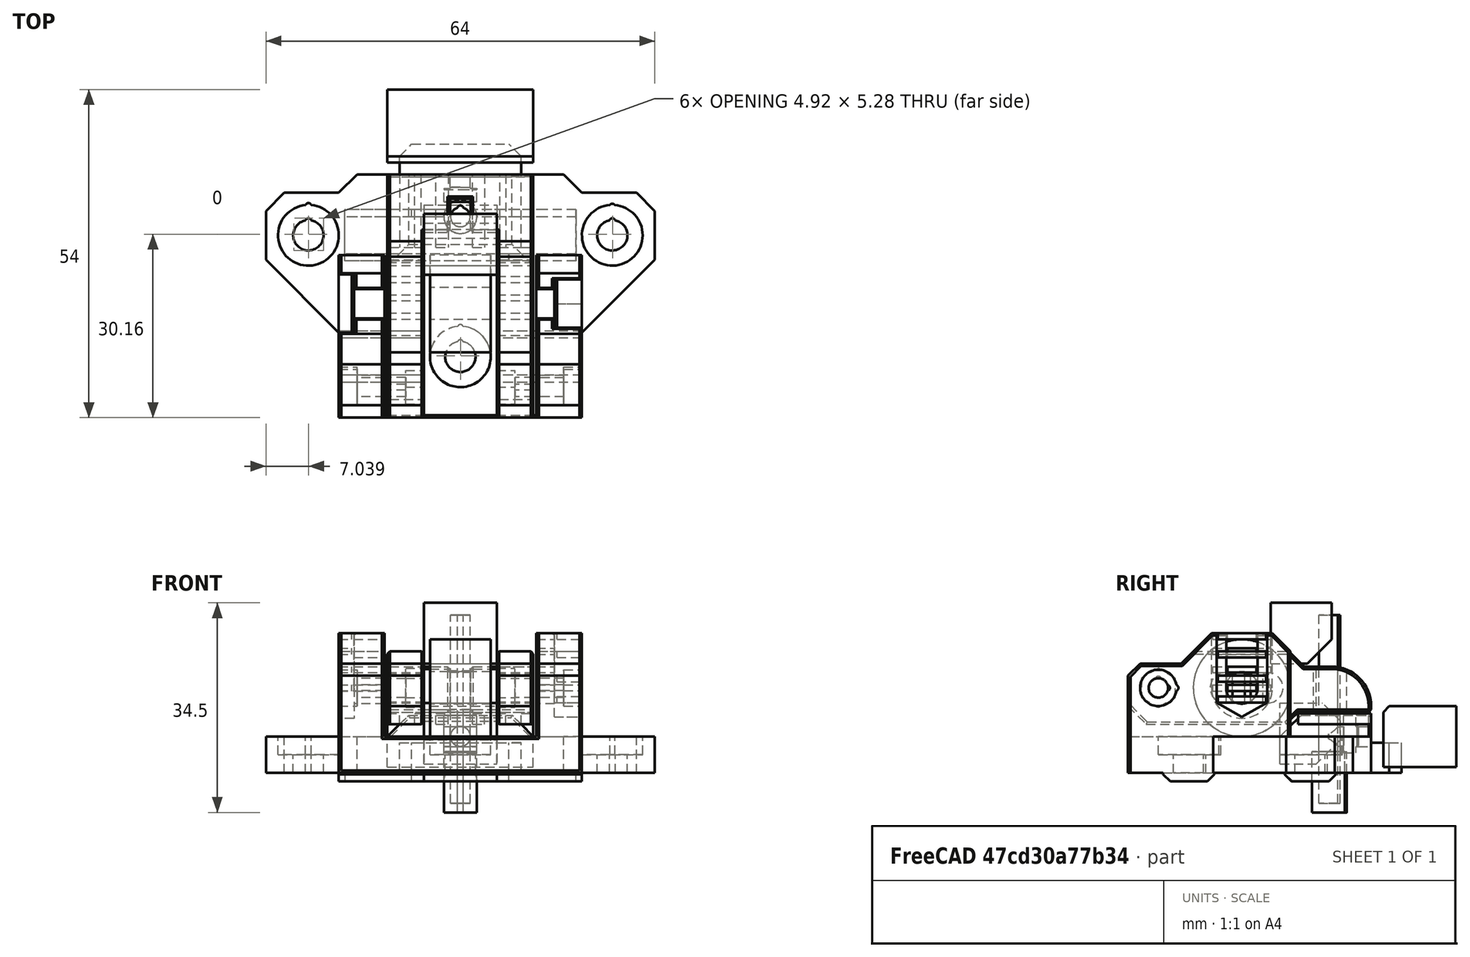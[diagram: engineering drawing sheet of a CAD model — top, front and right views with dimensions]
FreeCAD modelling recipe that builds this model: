
FCSTD DOCUMENT  (FreeCAD 0.18R14555 (Git shallow))
Label: y-idler-10mm-lower-rev
License: All rights reserved
LicenseURL: http://en.wikipedia.org/wiki/All_rights_reserved
objects: Part::Box×69, Part::Cylinder×39, Part::MultiFuse×35, Part::Cut×34, Part::Chamfer×25, Part::Feature×14, Part::Fillet×1
note: 217 computed .brp shape members not serialized (recipe doc carries the construction recipe); baked Part::Feature solids carry a one-line shape summary decoded from their .brp

FEATURE [Part::Box] Box  label="Cube"
  AttacherType = Attacher::AttachEngine3D
  Height = 10
  Length = 40
  Placement = pos=(-20,-20,-10) rot=(0,0,1;0rad)
  Width = 40
FEATURE [Part::Box] Box001  label="Cube001"
  AttacherType = Attacher::AttachEngine3D
  Height = 12
  Length = 6
  Placement = pos=(6,-20,4) rot=(0,0,1;0rad)
  Width = 43
FEATURE [Part::Box] Box002  label="Cube002"
  AttacherType = Attacher::AttachEngine3D
  Height = 12
  Length = 6
  Placement = pos=(-12,-20,4) rot=(0,0,1;0rad)
  Width = 43
FEATURE [Part::Box] Box003  label="Cube003"
  AttacherType = Attacher::AttachEngine3D
  Height = 12
  Length = 12
  Placement = pos=(-6,10.5,3) rot=(0,0,1;0rad)
  Width = 12.5
FEATURE [Part::Cylinder] Cylinder  label="idler"
  Angle = 360
  AttacherType = Attacher::AttachEngine3D
  Height = 10
  Placement = pos=(5,-1.25,10) rot=(0,-1,0;1.5708rad)
  Radius = 8
FEATURE [Part::Cylinder] Cylinder001
  Angle = 360
  AttacherType = Attacher::AttachEngine3D
  Height = 6
  Placement = pos=(6,-2,15) rot=(0,1,0;1.5708rad)
  Radius = 2.5
FEATURE [Part::Cylinder] Cylinder002
  Angle = 360
  AttacherType = Attacher::AttachEngine3D
  Height = 6
  Placement = pos=(-12,5,15) rot=(0,1,0;1.5708rad)
  Radius = 2.5
FEATURE [Part::Cylinder] Cylinder003
  Angle = 360
  AttacherType = Attacher::AttachEngine3D
  Height = 6
  Placement = pos=(-12,-2,15) rot=(0,1,0;1.5708rad)
  Radius = 2.5
FEATURE [Part::Cylinder] Cylinder004
  Angle = 360
  AttacherType = Attacher::AttachEngine3D
  Height = 6
  Placement = pos=(6,5,15) rot=(0,1,0;1.5708rad)
  Radius = 2.5
FEATURE [Part::Box] Box005  label="Cube005"
  AttacherType = Attacher::AttachEngine3D
  Height = 5
  Length = 6
  Placement = pos=(6,-2,12.5) rot=(0,0,1;0rad)
  Width = 7
FEATURE [Part::Box] Box006  label="Cube006"
  AttacherType = Attacher::AttachEngine3D
  Height = 5
  Length = 6
  Placement = pos=(-12,-2,12.5) rot=(0,0,1;0rad)
  Width = 7
FEATURE [Part::MultiFuse] Fusion
  Placement = pos=(0,-2,-5) rot=(0,0,1;0rad)
  Shapes = -> [Box005,Cylinder001,Cylinder004]
FEATURE [Part::MultiFuse] Fusion001
  Placement = pos=(0,-2,-5) rot=(0,0,1;0rad)
  Shapes = -> [Box006,Cylinder003,Cylinder002]
FEATURE [Part::Box] Box007  label="Cube007"
  AttacherType = Attacher::AttachEngine3D
  Height = 12
  Length = 7.5
  Placement = pos=(-20,-20,0) rot=(0,0,1;0rad)
  Width = 11
FEATURE [Part::Box] Box008  label="Cube008"
  AttacherType = Attacher::AttachEngine3D
  Height = 12
  Length = 7.5
  Placement = pos=(12.5,-20,0) rot=(0,0,1;0rad)
  Width = 11
FEATURE [Part::Box] Box009  label="Cube009"
  AttacherType = Attacher::AttachEngine3D
  Height = 20
  Length = 7.5
  Placement = pos=(-20,-10,0) rot=(0,0,1;0rad)
  Width = 18
FEATURE [Part::Box] Box010  label="Cube010"
  AttacherType = Attacher::AttachEngine3D
  Height = 20
  Length = 7.5
  Placement = pos=(12.5,-10,0) rot=(0,0,1;0rad)
  Width = 18
FEATURE [Part::Chamfer] Chamfer
  Base = -> Box009
  Edges = 2 edges r=4: [Edge10,Edge12]
FEATURE [Part::Chamfer] Chamfer001
  Base = -> Box010
  Edges = 2 edges r=4: [Edge10,Edge12]
FEATURE [Part::Cylinder] Cylinder005  label="Cylinder"
  Angle = 360
  AttacherType = Attacher::AttachEngine3D
  Height = 8
  Placement = pos=(-12,0,10) rot=(0,-1,0;1.5708rad)
  Radius = 2.6
FEATURE [Part::Cylinder] Cylinder006  label="Cylinder005"
  Angle = 360
  AttacherType = Attacher::AttachEngine3D
  Height = 8
  Placement = pos=(20,0,10) rot=(0,-1,0;1.5708rad)
  Radius = 2.6
FEATURE [Part::Box] Box011  label="Cube011"
  AttacherType = Attacher::AttachEngine3D
  Height = 10
  Length = 8
  Placement = pos=(12,-2.6,10) rot=(0,0,1;0rad)
  Width = 5.2
FEATURE [Part::Box] Box012  label="Cube012"
  AttacherType = Attacher::AttachEngine3D
  Height = 10
  Length = 8
  Placement = pos=(-20,-2.6,10) rot=(0,0,1;0rad)
  Width = 5.2
FEATURE [Part::Cylinder] Cylinder007  label="Cylinder006"
  Angle = 360
  AttacherType = Attacher::AttachEngine3D
  Height = 31
  Placement = pos=(0,16,-10) rot=(0,0,1;0rad)
  Radius = 1.6
FEATURE [Part::Cylinder] Cylinder008  label="Cylinder007"
  Angle = 360
  AttacherType = Attacher::AttachEngine3D
  Height = 3
  Placement = pos=(25,10,-3) rot=(0,0,1;0rad)
  Radius = 5
FEATURE [Part::Cylinder] Cylinder009  label="Cylinder008"
  Angle = 360
  AttacherType = Attacher::AttachEngine3D
  Height = 8
  Placement = pos=(-12,-15,10) rot=(0,-1,0;1.5708rad)
  Radius = 1.6
FEATURE [Part::Cylinder] Cylinder010  label="Cylinder009"
  Angle = 360
  AttacherType = Attacher::AttachEngine3D
  Height = 8
  Placement = pos=(20,-15,10) rot=(0,-1,0;1.5708rad)
  Radius = 1.6
FEATURE [Part::Cylinder] Cylinder011  label="Cylinder010"
  Angle = 360
  AttacherType = Attacher::AttachEngine3D
  Height = 24
  Placement = pos=(12,-15,10) rot=(0,-1,0;1.5708rad)
  Radius = 1.6
FEATURE [Part::Cylinder] Cylinder012  label="Cylinder011"
  Angle = 360
  AttacherType = Attacher::AttachEngine3D
  Height = 3
  Placement = pos=(-25,10,-3) rot=(0,0,1;0rad)
  Radius = 5
FEATURE [Part::Box] Box014  label="Cube014"
  AttacherType = Attacher::AttachEngine3D
  Height = 10
  Length = 64
  Placement = pos=(-32,-6,-10) rot=(0,0,1;0rad)
  Width = 23
FEATURE [Part::Chamfer] Chamfer004
  Base = -> Box014
  Edges = 2 edges r=12: [Edge1,Edge5]
FEATURE [Part::Chamfer] Chamfer005
  Base = -> Box
  Edges = 2 edges r=3: [Edge3,Edge7]
FEATURE [Part::Chamfer] Chamfer006
  Base = -> Chamfer004
  Edges = 2 edges r=3: [Edge3,Edge13]
FEATURE [Part::Cylinder] Cylinder013  label="Cylinder012"
  Angle = 360
  AttacherType = Attacher::AttachEngine3D
  Height = 24
  Placement = pos=(12,-15,11.4) rot=(0,-1,0;1.5708rad)
  Radius = 0.5
FEATURE [Part::Cylinder] Cylinder014  label="Cylinder013"
  Angle = 360
  AttacherType = Attacher::AttachEngine3D
  Height = 8
  Placement = pos=(20,-13.6,10) rot=(0,-1,0;1.5708rad)
  Radius = 0.5
FEATURE [Part::Cylinder] Cylinder015  label="Cylinder014"
  Angle = 360
  AttacherType = Attacher::AttachEngine3D
  Height = 8
  Placement = pos=(-12,-13.6,10) rot=(0,-1,0;1.5708rad)
  Radius = 0.5
FEATURE [Part::Cylinder] Cylinder016  label="Cylinder015"
  Angle = 360
  AttacherType = Attacher::AttachEngine3D
  Height = 15
  Placement = pos=(-25,10,-10) rot=(0,0,1;0rad)
  Radius = 2.5
FEATURE [Part::Cylinder] Cylinder017  label="Cylinder016"
  Angle = 360
  AttacherType = Attacher::AttachEngine3D
  Height = 15
  Placement = pos=(25,10,-10) rot=(0,0,1;0rad)
  Radius = 2.5
FEATURE [Part::Cylinder] Cylinder018  label="Cylinder019"
  Angle = 360
  AttacherType = Attacher::AttachEngine3D
  Height = 15
  Placement = pos=(25,12.3,-10) rot=(0,0,1;0rad)
  Radius = 0.5
FEATURE [Part::Cylinder] Cylinder019  label="Cylinder020"
  Angle = 360
  AttacherType = Attacher::AttachEngine3D
  Height = 15
  Placement = pos=(-25,12.3,-10) rot=(0,0,1;0rad)
  Radius = 0.5
FEATURE [Part::Cylinder] Cylinder020  label="Cylinder021"
  Angle = 360
  AttacherType = Attacher::AttachEngine3D
  Height = 31
  Placement = pos=(0,17.4,-10) rot=(0,0,1;0rad)
  Radius = 0.5
FEATURE [Part::Cylinder] Cylinder021  label="Cylinder022"
  Angle = 360
  AttacherType = Attacher::AttachEngine3D
  Height = 15
  Placement = pos=(0,-10,-10) rot=(0,0,1;0rad)
  Radius = 2.5
FEATURE [Part::Cylinder] Cylinder023  label="Cylinder024"
  Angle = 360
  AttacherType = Attacher::AttachEngine3D
  Height = 15
  Placement = pos=(0,-7.7,-10) rot=(0,0,1;0rad)
  Radius = 0.5
FEATURE [Part::Cylinder] Cylinder024  label="Cylinder025"
  Angle = 360
  AttacherType = Attacher::AttachEngine3D
  Height = 2.5
  Placement = pos=(-17.5,0,10) rot=(0,-1,0;1.5708rad)
  Radius = 5
FEATURE [Part::Box] Box015  label="Cube015"
  AttacherType = Attacher::AttachEngine3D
  Height = 10
  Length = 2.5
  Placement = pos=(-20,-5,10) rot=(0,0,1;0rad)
  Width = 10
FEATURE [Part::Feature] Fusion010001  label="Fusion011"
  Placement = pos=(0,5.775,5) rot=(0,0,1;0rad)
  shape: bbox 40 x 8.45 x 1.4 mm, 38 faces (baked)
FEATURE [Part::Feature] Fusion010002  label="Fusion012"
  Placement = pos=(12,25.77,5) rot=(0,0,1;0rad)
  shape: bbox 40 x 8.45 x 1.4 mm, 38 faces (baked)
FEATURE [Part::Feature] Fusion010003  label="Fusion013"
  Placement = pos=(-12,25.765,5) rot=(0,0,1;0rad)
  shape: bbox 40 x 8.45 x 1.4 mm, 38 faces (baked)
FEATURE [Part::Cylinder] Cylinder025  label="Cylinder026"
  Angle = 360
  AttacherType = Attacher::AttachEngine3D
  Height = 3
  Placement = pos=(0,-10,-3) rot=(0,0,1;0rad)
  Radius = 5
FEATURE [Part::Cylinder] Cylinder026  label="Cylinder027"
  Angle = 360
  AttacherType = Attacher::AttachEngine3D
  Height = 3
  Placement = pos=(0,-5.2,-3) rot=(0,0,1;0rad)
  Radius = 0.5
FEATURE [Part::Cylinder] Cylinder027  label="Cylinder028"
  Angle = 360
  AttacherType = Attacher::AttachEngine3D
  Height = 3
  Placement = pos=(-25,14.8,-3) rot=(0,0,1;0rad)
  Radius = 0.5
FEATURE [Part::Cylinder] Cylinder028  label="Cylinder029"
  Angle = 360
  AttacherType = Attacher::AttachEngine3D
  Height = 3
  Placement = pos=(25,14.7,-3) rot=(0,0,1;0rad)
  Radius = 0.5
FEATURE [Part::MultiFuse] Fusion010005
  Shapes = -> [Cylinder025,Cylinder012,Cylinder008]
FEATURE [Part::Box] Box017  label="Cube017"
  AttacherType = Attacher::AttachEngine3D
  Height = 10
  Length = 10
  Placement = pos=(-60,0,-20) rot=(0,0,1;0rad)
  Width = 10
FEATURE [Part::Box] Box018  label="Cube018"
  AttacherType = Attacher::AttachEngine3D
  Height = 10
  Length = 10
  Placement = pos=(-40,0,-20) rot=(0,0,1;0rad)
  Width = 10
FEATURE [Part::Box] Box019  label="Cube019"
  AttacherType = Attacher::AttachEngine3D
  Height = 10
  Length = 10
  Placement = pos=(40,0,-20) rot=(0,0,1;0rad)
  Width = 10
FEATURE [Part::Box] Box020  label="Cube020"
  AttacherType = Attacher::AttachEngine3D
  Height = 10
  Length = 10
  Placement = pos=(40,0,-20) rot=(0,0,1;0rad)
  Width = 10
FEATURE [Part::Chamfer] Chamfer016
  Base = -> Box018
  Edges = 1 edges r=4: [Edge5]
  Placement = pos=(0,12,5) rot=(0,0,1;0rad)
FEATURE [Part::Chamfer] Chamfer017
  Base = -> Box017
  Edges = 1 edges r=4: [Edge7]
  Placement = pos=(20,-2,5) rot=(0,0,1;0rad)
FEATURE [Part::Chamfer] Chamfer018
  Base = -> Box019
  Edges = 1 edges r=4: [Edge3]
  Placement = pos=(-11,-3,5) rot=(0,0,1;0rad)
FEATURE [Part::Chamfer] Chamfer019
  Base = -> Box020
  Edges = 1 edges r=4: [Edge1]
  Placement = pos=(-9,11,5) rot=(0,0,1;0rad)
FEATURE [Part::Cylinder] Cylinder030  label="Cylinder031"
  Angle = 360
  AttacherType = Attacher::AttachEngine3D
  Height = 3
  Placement = pos=(-20,-12.2,10) rot=(0,1,0;1.5708rad)
  Radius = 0.5
FEATURE [Part::Cylinder] Cylinder031  label="Cylinder032"
  Angle = 360
  AttacherType = Attacher::AttachEngine3D
  Height = 3
  Placement = pos=(-20,-15,10) rot=(0,1,0;1.5708rad)
  Radius = 3
FEATURE [Part::Feature] Body005001  label="Body006"
  Placement = pos=(-9,-15,10) rot=(1,0,0;1.5708rad)
  shape: bbox 3 x 5.543 x 6.4 mm, 8 faces (baked)
FEATURE [Part::Cylinder] Cylinder032  label="Cylinder033"
  Angle = 360
  AttacherType = Attacher::AttachEngine3D
  Height = 3
  Placement = pos=(17,-15,10) rot=(0,1,0;1.5708rad)
  Radius = 3
FEATURE [Part::Cylinder] Cylinder033  label="Cylinder034"
  Angle = 360
  AttacherType = Attacher::AttachEngine3D
  Height = 3
  Placement = pos=(17,-12.2,10) rot=(0,1,0;1.5708rad)
  Radius = 0.5
FEATURE [Part::MultiFuse] Fusion010006003
  Shapes = -> [Cylinder031,Cylinder030]
FEATURE [Part::MultiFuse] Fusion010006004
  Shapes = -> [Cylinder033,Cylinder032]
FEATURE [Part::Feature] Body005002  label="Body007"
  Placement = pos=(6,-15,10) rot=(1,0,0;1.5708rad)
  shape: bbox 3 x 5.543 x 6.4 mm, 8 faces (baked)
FEATURE [Part::Box] Box029  label="Cube029"
  AttacherType = Attacher::AttachEngine3D
  Height = 1
  Length = 2.1
  Placement = pos=(-20,-3.53,7.5) rot=(0,0,1;0rad)
  Width = 9.6
FEATURE [Part::Box] Box030  label="Cube030"
  AttacherType = Attacher::AttachEngine3D
  Height = 1
  Length = 4.1
  Placement = pos=(15.9,-2.68,5.6) rot=(0,0,1;0rad)
  Width = 7.91
FEATURE [Part::Box] Box032  label="Cube032"
  AttacherType = Attacher::AttachEngine3D
  Height = 1
  Length = 5
  Placement = pos=(-17.5,-1.13,7.5) rot=(0,0,1;0rad)
  Width = 4.8
FEATURE [Part::MultiFuse] Fusion010006008
  Shapes = -> [Box012,Cylinder005]
FEATURE [Part::MultiFuse] Fusion010006009
  Shapes = -> [Cylinder006,Box011]
FEATURE [Part::Cut] Cut022015
  Base = -> Chamfer
  Tool = -> Fusion010006008
FEATURE [Part::Cut] Cut022016
  Base = -> Chamfer001
  Tool = -> Fusion010006009
FEATURE [Part::Feature] Pad002001  label="Pad003"
  Placement = pos=(17.5,0,10) rot=(0.57735,0.57735,0.57735;2.0944rad)
  shape: bbox 10 x 8.314 x 9.6 mm, 8 faces (baked)
FEATURE [Part::Feature] Pad002002  label="Pad004"
  Placement = pos=(17.5,0,14) rot=(0.57735,0.57735,0.57735;2.0944rad)
  shape: bbox 10 x 8.314 x 9.6 mm, 8 faces (baked)
FEATURE [Part::Feature] Pad002003  label="Pad005"
  Placement = pos=(17.5,0,18) rot=(0.57735,0.57735,0.57735;2.0944rad)
  shape: bbox 10 x 8.314 x 9.6 mm, 8 faces (baked)
FEATURE [Part::MultiFuse] Fusion010006010
  Shapes = -> [Pad002003,Pad002001,Pad002002]
FEATURE [Part::Cut] Cut022017  label="base-right-arm-top"
  Base = -> Cut022016
  Placement = pos=(0,1.27,-2) rot=(0,0,1;0rad)
  Tool = -> Fusion010006010
FEATURE [Part::MultiFuse] Fusion010006011
  Shapes = -> [Cylinder024,Box015]
FEATURE [Part::Cut] Cut022018  label="base-left-arm-top"
  Base = -> Cut022015
  Placement = pos=(0,1.27,-2) rot=(0,0,1;0rad)
  Tool = -> Fusion010006011
FEATURE [Part::MultiFuse] Fusion010006014
  Shapes = -> [Cylinder013,Cylinder011]
FEATURE [Part::MultiFuse] Fusion010006015
  Placement = pos=(0,0,-1) rot=(0,0,1;0rad)
  Shapes = -> [Fusion010006014,Body005002,Body005001]
FEATURE [Part::MultiFuse] Fusion010006012003
  Placement = pos=(0,0,-2) rot=(0,0,1;0rad)
  Shapes = -> [Fusion010006003,Cylinder015,Cylinder009]
FEATURE [Part::MultiFuse] Fusion010006012004
  Placement = pos=(0,0,-2) rot=(0,0,1;0rad)
  Shapes = -> [Cylinder010,Cylinder014,Fusion010006004]
FEATURE [Part::MultiFuse] Fusion010006012005
  Placement = pos=(0,0,5) rot=(0,0,1;0rad)
  Shapes = -> [Chamfer006,Chamfer005]
FEATURE [Part::Box] Box038  label="Cube038"
  AttacherType = Attacher::AttachEngine3D
  Height = 5
  Length = 65
  Placement = pos=(-32,-24,1) rot=(0,0,1;0rad)
  Width = 50
FEATURE [Part::MultiFuse] Fusion010006012007
  Shapes = -> [Chamfer018,Chamfer019,Chamfer016,Chamfer017]
FEATURE [Part::MultiFuse] Fusion010006012008
  Placement = pos=(0,0,1) rot=(0,0,1;0rad)
  Shapes = -> [Fusion010005,Cylinder027,Cylinder028,Cylinder026]
FEATURE [Part::Box] Box039  label="Cube039"
  AttacherType = Attacher::AttachEngine3D
  Height = 10
  Length = 40
  Placement = pos=(-26,-25,12) rot=(0,0,1;0rad)
  Width = 20
FEATURE [Part::Chamfer] Chamfer027
  Base = -> Box039
  Edges = 1 edges r=2: [Edge11]
  Placement = pos=(0,-4.25,1) rot=(0,0,1;0rad)
FEATURE [Part::Box] Box040  label="Cube040"
  AttacherType = Attacher::AttachEngine3D
  Height = 10
  Length = 32
  Placement = pos=(-15,24,-8) rot=(0,0,1;0rad)
  Width = 26
FEATURE [Part::Chamfer] Chamfer028
  Base = -> Box040
  Edges = 1 edges r=3: [Edge10]
  Placement = pos=(0,-19,3) rot=(0,0,1;0rad)
FEATURE [Part::Box] Box043  label="cube042"
  AttacherType = Attacher::AttachEngine3D
  Height = 2.8
  Length = 2
  Placement = pos=(-12,11,2) rot=(0,0,1;0rad)
  Width = 12
FEATURE [Part::Box] Box044  label="Cube043"
  AttacherType = Attacher::AttachEngine3D
  Height = 4.6
  Length = 6
  Placement = pos=(-12,-2,5.7) rot=(0,0,1;0rad)
  Width = 1
FEATURE [Part::Box] Box045  label="Cube044"
  AttacherType = Attacher::AttachEngine3D
  Height = 4.6
  Length = 6
  Placement = pos=(6,-2,5.7) rot=(0,0,1;0rad)
  Width = 1
FEATURE [Part::Box] Box052  label="Cube047"
  AttacherType = Attacher::AttachEngine3D
  Height = 4.6
  Length = 6
  Placement = pos=(-12,1,5.7) rot=(0,0,1;0rad)
  Width = 1
FEATURE [Part::Box] Box054  label="Cube049"
  AttacherType = Attacher::AttachEngine3D
  Height = 4.6
  Length = 6
  Placement = pos=(-12,4,5.7) rot=(0,0,1;0rad)
  Width = 1
FEATURE [Part::Box] Box055  label="Cube050"
  AttacherType = Attacher::AttachEngine3D
  Height = 4.6
  Length = 6
  Placement = pos=(6,1,5.7) rot=(0,0,1;0rad)
  Width = 1
FEATURE [Part::Box] Box057  label="Cube052"
  AttacherType = Attacher::AttachEngine3D
  Height = 4.6
  Length = 6
  Placement = pos=(6,4,5.7) rot=(0,0,1;0rad)
  Width = 1
FEATURE [Part::Box] Box058  label="Cube053"
  AttacherType = Attacher::AttachEngine3D
  Height = 1
  Length = 4.1
  Placement = pos=(15.9,-2.68,9) rot=(0,0,1;0rad)
  Width = 7.91
FEATURE [Part::Box] Box059  label="Cube054"
  AttacherType = Attacher::AttachEngine3D
  Height = 1
  Length = 3
  Placement = pos=(12.5,-1.13,7.5) rot=(0,0,1;0rad)
  Width = 4.8
FEATURE [Part::Box] Box063  label="Cube058"
  AttacherType = Attacher::AttachEngine3D
  Height = 1
  Length = 3
  Placement = pos=(12.5,-1.13,10.5) rot=(0,0,1;0rad)
  Width = 4.8
FEATURE [Part::Box] Box064  label="Cube059"
  AttacherType = Attacher::AttachEngine3D
  Height = 1
  Length = 2.1
  Placement = pos=(-20,-3.53,10.5) rot=(0,0,1;0rad)
  Width = 9.6
FEATURE [Part::Box] Box066  label="Cube061"
  AttacherType = Attacher::AttachEngine3D
  Height = 1
  Length = 5
  Placement = pos=(-17.5,-1.13,10.5) rot=(0,0,1;0rad)
  Width = 4.8
FEATURE [Part::Box] Box068  label="Cube063"
  AttacherType = Attacher::AttachEngine3D
  Height = 1
  Length = 3
  Placement = pos=(12.5,-1.13,13.5) rot=(0,0,1;0rad)
  Width = 4.8
FEATURE [Part::Box] Box069  label="Cube064"
  AttacherType = Attacher::AttachEngine3D
  Height = 1
  Length = 2.1
  Placement = pos=(-20,-3.53,13.5) rot=(0,0,1;0rad)
  Width = 9.6
FEATURE [Part::Box] Box070  label="Cube065"
  AttacherType = Attacher::AttachEngine3D
  Height = 1
  Length = 2.1
  Placement = pos=(-20,-3.53,16) rot=(0,0,1;0rad)
  Width = 9.6
FEATURE [Part::Box] Box071  label="Cube066"
  AttacherType = Attacher::AttachEngine3D
  Height = 1
  Length = 5
  Placement = pos=(-17.5,-1.13,16) rot=(0,0,1;0rad)
  Width = 4.8
FEATURE [Part::Box] Box075  label="Cube070"
  AttacherType = Attacher::AttachEngine3D
  Height = 1
  Length = 3
  Placement = pos=(12.5,-1.13,16) rot=(0,0,1;0rad)
  Width = 4.8
FEATURE [Part::Box] Box076  label="Cube071"
  AttacherType = Attacher::AttachEngine3D
  Height = 1
  Length = 5
  Placement = pos=(-17.5,-1.13,13) rot=(0,0,1;0rad)
  Width = 4.8
FEATURE [Part::Box] Box077  label="Cube072"
  AttacherType = Attacher::AttachEngine3D
  Height = 1
  Length = 4.1
  Placement = pos=(15.9,-2.68,16) rot=(0,0,1;0rad)
  Width = 7.91
FEATURE [Part::Box] Box078  label="Cube073"
  AttacherType = Attacher::AttachEngine3D
  Height = 1
  Length = 4.1
  Placement = pos=(15.9,-2.68,13) rot=(0,0,1;0rad)
  Width = 7.91
FEATURE [Part::Box] Box079  label="Cube074"
  AttacherType = Attacher::AttachEngine3D
  Height = 17
  Length = 10
  Placement = pos=(-21,-15,0) rot=(0,0,1;0rad)
  Width = 14
FEATURE [Part::Chamfer] Chamfer030006
  Base = -> Box079
  Edges = 1 edges r=10: [Edge11]
  Placement = pos=(0,2.27,12) rot=(0,0,1;0rad)
FEATURE [Part::Feature] Chamfer030006001  label="Chamfer030007"
  Placement = pos=(32,2.27,12) rot=(0,0,1;0rad)
  shape: bbox 10 x 14 x 17 mm, 7 faces (baked)
FEATURE [Part::Cut] Cut022020016004
  Base = -> Cut022018
  Tool = -> Chamfer030006
FEATURE [Part::Cut] Cut022020016005
  Base = -> Cut022017
  Tool = -> Chamfer030006001
FEATURE [Part::Box] Box080  label="Cube075"
  AttacherType = Attacher::AttachEngine3D
  Height = 10
  Length = 12
  Placement = pos=(-21,-5,17) rot=(0,0,1;0rad)
  Width = 16
FEATURE [Part::Cut] Cut022020016006  label="base-left-arm-top-trim"
  Base = -> Cut022020016004
  Placement = pos=(0,-2.52,1) rot=(0,0,1;0rad)
  Tool = -> Box080
FEATURE [Part::Box] Box081  label="Cube076"
  AttacherType = Attacher::AttachEngine3D
  Height = 10
  Length = 12
  Placement = pos=(9,-5,17) rot=(0,0,1;0rad)
  Width = 16
FEATURE [Part::Cut] Cut022020016007  label="base-right-arm-top-trim"
  Base = -> Cut022020016005
  Placement = pos=(0,2.54,0) rot=(0,0,1;0rad)
  Tool = -> Box081
FEATURE [Part::MultiFuse] Fusion010006012010005014
  Shapes = -> [Box071,Box076,Box066,Box032]
FEATURE [Part::MultiFuse] Fusion010006012010005016
  Shapes = -> [Box029,Box064,Box069,Box070]
FEATURE [Part::Box] Box082  label="Cube077"
  AttacherType = Attacher::AttachEngine3D
  Height = 14
  Length = 2
  Placement = pos=(17.55,-3.1,3) rot=(0,0,1;0rad)
  Width = 9
FEATURE [Part::Feature] Chamfer030006002001  label="arm-rev-4-3-no-support001"
  shape: bbox 64 x 40 x 23.4 mm, 138 faces (baked)
FEATURE [Part::Cut] Cut022020016008
  Base = -> Box082
  Placement = pos=(-2.05,2.54,0) rot=(0,0,1;0rad)
  Tool = -> Chamfer030006002001
FEATURE [Part::MultiFuse] Fusion010006012010005012002
  Shapes = -> [Box059,Box075,Box063,Box068]
FEATURE [Part::MultiFuse] Fusion010006012010005012003
  Shapes = -> [Box030,Box078,Box058,Box077]
FEATURE [Part::MultiFuse] Fusion010006012010005012004  label="base-custom-support"
  Placement = pos=(0,-2.52,1) rot=(0,0,1;0rad)
  Shapes = -> [Fusion010006012010005016,Fusion010006012010005012002,Fusion010006012010005012003,Fusion010006012010005014]
FEATURE [Part::Box] Box083  label="Cube078"
  AttacherType = Attacher::AttachEngine3D
  Height = 10
  Length = 12
  Placement = pos=(-6,-15,-15) rot=(0,0,1;0rad)
  Width = 10
FEATURE [Part::Box] Box084  label="Cube079"
  AttacherType = Attacher::AttachEngine3D
  Height = 10
  Length = 13
  Placement = pos=(19,5,-15) rot=(0,0,1;0rad)
  Width = 10
FEATURE [Part::Box] Box085  label="Cube080"
  AttacherType = Attacher::AttachEngine3D
  Height = 10
  Length = 13
  Placement = pos=(-32,5,-15) rot=(0,0,1;0rad)
  Width = 10
FEATURE [Part::Cut] Cut022020016019  label="base-right-arm-top-cut"
  Base = -> Cut022020016007
  Placement = pos=(0,-5.06,1) rot=(0,0,1;0rad)
  Tool = -> Cut022020016008
FEATURE [Part::Cylinder] Cylinder038  label="Cylinder039"
  Angle = 360
  AttacherType = Attacher::AttachEngine3D
  Height = 10
  Placement = pos=(0,13,-11.5) rot=(0,0,1;0rad)
  Radius = 2.7
FEATURE [Part::Cylinder] Cylinder039  label="Cylinder040"
  Angle = 360
  AttacherType = Attacher::AttachEngine3D
  Height = 10
  Placement = pos=(0,15.5,-11.5) rot=(0,0,1;0rad)
  Radius = 0.5
FEATURE [Part::Box] Box087  label="cube043"
  AttacherType = Attacher::AttachEngine3D
  Height = 2.8
  Length = 1
  Placement = pos=(-7.5,11,2) rot=(0,0,1;0rad)
  Width = 12
FEATURE [Part::Box] Box089  label="cube045"
  AttacherType = Attacher::AttachEngine3D
  Height = 2.8
  Length = 2
  Placement = pos=(-4,11,2) rot=(0,0,1;0rad)
  Width = 12
FEATURE [Part::Box] Box090  label="cube046"
  AttacherType = Attacher::AttachEngine3D
  Height = 2.8
  Length = 2
  Placement = pos=(10,11,2) rot=(0,0,1;0rad)
  Width = 12
FEATURE [Part::Box] Box091  label="cube047"
  AttacherType = Attacher::AttachEngine3D
  Height = 2.8
  Length = 1
  Placement = pos=(6.5,11,2) rot=(0,0,1;0rad)
  Width = 12
FEATURE [Part::Box] Box093  label="cube049"
  AttacherType = Attacher::AttachEngine3D
  Height = 2.8
  Length = 2
  Placement = pos=(2,11,2) rot=(0,0,1;0rad)
  Width = 12
FEATURE [Part::Box] Box095  label="Cube083"
  AttacherType = Attacher::AttachEngine3D
  Height = 5
  Length = 20
  Placement = pos=(-10,20,-5) rot=(0,0,1;0rad)
  Width = 5
FEATURE [Part::Chamfer] Chamfer030006002012
  Base = -> Box095
  Edges = 2 edges r=2: [Edge3,Edge7]
FEATURE [Part::MultiFuse] Fusion010006012010005012005015
  Placement = pos=(0,1.5,1) rot=(0,0,1;0rad)
  Shapes = -> [Box090,Box091,Box093,Box089,Box087,Box043]
FEATURE [Part::MultiFuse] Fusion010006012010005012005016
  Placement = pos=(0,-1.79,1) rot=(0,0,1;0rad)
  Shapes = -> [Box045,Box055,Box057]
FEATURE [Part::MultiFuse] Fusion010006012010005012005017
  Placement = pos=(0,-1.79,1) rot=(0,0,1;0rad)
  Shapes = -> [Box052,Box054,Box044]
FEATURE [Part::Box] Box096  label="Cube084"
  AttacherType = Attacher::AttachEngine3D
  Height = 10
  Length = 12
  Placement = pos=(-6,0,12) rot=(0,0,1;0rad)
  Width = 10
FEATURE [Part::Chamfer] Chamfer030006002016
  Base = -> Box096
  Edges = 1 edges r=4: [Edge11]
  Placement = pos=(0,3.5,1) rot=(0,0,1;0rad)
FEATURE [Part::Cylinder] Cylinder040  label="Cylinder041"
  Angle = 360
  AttacherType = Attacher::AttachEngine3D
  Height = 5
  Placement = pos=(0,16,-5) rot=(0,0,1;0rad)
  Radius = 3.1
FEATURE [Part::Box] Box098  label="Cube086"
  AttacherType = Attacher::AttachEngine3D
  Height = 7
  Length = 5.4
  Placement = pos=(-2.7,18.5,-1.7) rot=(0,0,1;0rad)
  Width = 2.4
FEATURE [Part::Cylinder] Cylinder041  label="Cylinder042"
  Angle = 360
  AttacherType = Attacher::AttachEngine3D
  Height = 27
  Placement = pos=(0,16,-9) rot=(0,0,1;0rad)
  Radius = 1.6
FEATURE [Part::Cylinder] Cylinder042  label="Cylinder043"
  Angle = 360
  AttacherType = Attacher::AttachEngine3D
  Height = 27
  Placement = pos=(0,17.4,-9) rot=(0,0,1;0rad)
  Radius = 0.5
FEATURE [Part::MultiFuse] Fusion010006012010005012005020  label="screw-hole-cut"
  Placement = pos=(0,-3,0) rot=(0,0,1;0rad)
  Shapes = -> [Cylinder040,Cylinder042,Cylinder041]
FEATURE [Part::Cylinder] Cylinder043  label="Cylinder044"
  Angle = 360
  AttacherType = Attacher::AttachEngine3D
  Height = 18
  Placement = pos=(0,16,1) rot=(-1,0,0;1.5708rad)
  Radius = 1.65
FEATURE [Part::Box] Box099  label="Cube087"
  AttacherType = Attacher::AttachEngine3D
  Height = 6.5
  Length = 1.35
  Placement = pos=(-3,20.7,-2) rot=(0,0,1;0rad)
  Width = 0.2
FEATURE [Part::Box] Box100  label="Cube088"
  AttacherType = Attacher::AttachEngine3D
  Height = 6.5
  Length = 1.35
  Placement = pos=(1.65,20.7,-2) rot=(0,0,1;0rad)
  Width = 0.2
FEATURE [Part::Box] Box101  label="Cube089"
  AttacherType = Attacher::AttachEngine3D
  Height = 1.35
  Length = 6
  Placement = pos=(-3,20.5,-2) rot=(0,0,1;0rad)
  Width = 0.4
FEATURE [Part::Box] Box102  label="Cube090"
  AttacherType = Attacher::AttachEngine3D
  Height = 1.85
  Length = 6
  Placement = pos=(-3,20.5,2.65) rot=(0,0,1;0rad)
  Width = 0.4
FEATURE [Part::MultiFuse] Fusion010006012010005012005024
  Shapes = -> [Box101,Box099,Box100,Box102]
FEATURE [Part::Cut] Cut022020016032007004
  Base = -> Box098
  Tool = -> Fusion010006012010005012005024
FEATURE [Part::MultiFuse] Fusion010006012010005012005025  label="grub-screw-hole-cut"
  Placement = pos=(0,-3,0) rot=(0,0,1;0rad)
  Shapes = -> [Cut022020016032007004,Cylinder043]
FEATURE [Part::Box] Box103  label="Cube091"
  AttacherType = Attacher::AttachEngine3D
  Height = 30
  Length = 3.4
  Placement = pos=(-1.7,9,0) rot=(0,0,1;0rad)
  Width = 7
FEATURE [Part::Feature] Chamfer030006002016001  label="Chamfer030006002025"
  Placement = pos=(0,5.5,-22.5) rot=(0,0,1;0rad)
  shape: bbox 12 x 10 x 10 mm, 7 faces (baked)
FEATURE [Part::Chamfer] Chamfer030006002016002
  Base = -> Chamfer030006002016001
  Edges = 1 edges r=3: [Edge8]
  Placement = pos=(0,-0.5,7) rot=(0,0,1;0rad)
FEATURE [Part::Box] Box105  label="Cube093"
  AttacherType = Attacher::AttachEngine3D
  Height = 10
  Length = 24
  Placement = pos=(-12,17,0) rot=(0,0,1;0rad)
  Width = 12
FEATURE [Part::Chamfer] Chamfer030006002016005006
  Base = -> Box105
  Edges = 1 edges r=1: [Edge10]
  Placement = pos=(0,5,-4) rot=(0,0,1;0rad)
FEATURE [Part::Cut] Cut022020016032007025
  Base = -> Box007
  Tool = -> Fusion010006012003
FEATURE [Part::Cut] Cut022020016032007026
  Base = -> Box008
  Tool = -> Fusion010006012004
FEATURE [Part::Chamfer] Chamfer030006002016005008003003  label="base-right-arm-bottom"
  Base = -> Cut022020016032007026
  Edges = 1 edges r=2: [Edge10]
  Placement = pos=(0,0,1) rot=(0,0,1;0rad)
FEATURE [Part::Chamfer] Chamfer030006002016005008003004  label="base-left-arm-bottom"
  Base = -> Cut022020016032007025
  Edges = 1 edges r=2: [Edge10]
  Placement = pos=(0,0,1) rot=(0,0,1;0rad)
FEATURE [Part::Cut] Cut022020016032007027
  Base = -> Fusion010006012005
  Tool = -> Box038
FEATURE [Part::Cut] Cut022020016032007028
  Base = -> Cut022020016032007027
  Tool = -> Fusion010006012007
FEATURE [Part::MultiFuse] Fusion010006012010005012005027003
  Shapes = -> [Fusion010003,Fusion010001,Fusion010002,Cut022020016032007028]
FEATURE [Part::Cut] Cut022020016032007029
  Base = -> Fusion010006012010005012005027003
  Tool = -> Box085
FEATURE [Part::Cut] Cut022020016032007030
  Base = -> Cut022020016032007029
  Tool = -> Box083
FEATURE [Part::Cut] Cut022020016032007031
  Base = -> Cut022020016032007030
  Tool = -> Box084
FEATURE [Part::Cut] Cut
  Base = -> Box002
  Placement = pos=(0,0,-1) rot=(0,0,1;0rad)
  Tool = -> Fusion001
FEATURE [Part::Cut] Cut022020016032007036002
  Base = -> Box001
  Placement = pos=(0,0,-1) rot=(0,0,1;0rad)
  Tool = -> Fusion
FEATURE [Part::Box] Box106  label="Cube094"
  AttacherType = Attacher::AttachEngine3D
  Height = 10
  Length = 24
  Placement = pos=(-12,10.5,12.5) rot=(0,0,1;0rad)
  Width = 21
FEATURE [Part::Chamfer] Chamfer030006002016005008003006
  Base = -> Box106
  Edges = 1 edges r=3: [Edge9]
  Placement = pos=(0,-4.5,0) rot=(0,0,1;0rad)
FEATURE [Part::MultiFuse] Fusion010006012010005012005027007
  Shapes = -> [Cut,Box003,Cut022020016032007036002]
FEATURE [Part::Cut] Cut022020016032007036009
  Base = -> Fusion010006012010005012005027007
  Tool = -> Fusion010006015
FEATURE [Part::Box] Box107  label="Cube095"
  AttacherType = Attacher::AttachEngine3D
  Height = 10
  Length = 24
  Placement = pos=(-12,12,4.8) rot=(0,0,1;0rad)
  Width = 13
FEATURE [Part::MultiFuse] Fusion010006012010005012005027010
  Shapes = -> [Cylinder021,Cylinder023,Cylinder016,Cylinder019,Cylinder017,Cylinder018]
FEATURE [Part::Cut] Cut022020016032007036015
  Base = -> Cut022020016032007031
  Tool = -> Fusion010006012010005012005027010
FEATURE [Part::Cut] Cut022020016032007036016
  Base = -> Cut022020016032007036015
  Tool = -> Fusion010006012008
FEATURE [Part::MultiFuse] Fusion010006012010005012005027011
  Placement = pos=(0,-3,0) rot=(0,0,1;0rad)
  Shapes = -> [Cylinder007,Cylinder020]
FEATURE [Part::Box] Box108  label="Cube096"
  AttacherType = Attacher::AttachEngine3D
  Height = 9.5
  Length = 24
  Placement = pos=(-12,5,-5) rot=(0,0,1;0rad)
  Width = 15
FEATURE [Part::Chamfer] Chamfer030006002016005008003009003
  Base = -> Box108
  Edges = 3 edges r=3.5: [Edge2,Edge6,Edge10]
FEATURE [Part::Chamfer] Chamfer030006002016005008003009004
  Base = -> Chamfer030006002016005008003009003
  Edges = 3 edges r=0.4: [Edge10,Edge14,Edge15]
FEATURE [Part::MultiFuse] Fusion010006012010005012005027012
  Shapes = -> [Cylinder038,Cylinder039]
FEATURE [Part::Feature] Fusion010006012010005012005027011001  label="Fusion010006012010005012005027013"
  Placement = pos=(0,-3,0) rot=(0,0,1;0rad)
  shape: bbox 3.2 x 3.5 x 31 mm, 9 faces (baked)
FEATURE [Part::Cut] Cut022020016032007036017
  Base = -> Cut022020016032007036016
  Tool = -> Fusion010006012010005012005027011
FEATURE [Part::Feature] Fusion010006012010005012005027012001  label="Fusion010006012010005012005027014"
  shape: bbox 5.4 x 5.7 x 10 mm, 9 faces (baked)
FEATURE [Part::Cut] Cut022020016032007036018
  Base = -> Cut022020016032007036017
  Tool = -> Fusion010006012010005012005027012
FEATURE [Part::Cut] Cut022020016032007036019
  Base = -> Chamfer030006002016005008003009004
  Tool = -> Fusion010006012010005012005020
FEATURE [Part::MultiFuse] Fusion010006012010005012005027012002
  Shapes = -> [Cut022020016032007036018,Cut022020016032007036019]
FEATURE [Part::Cut] Cut022020016032007036020
  Base = -> Fusion010006012010005012005027012002
  Tool = -> Fusion010006012010005012005025
FEATURE [Part::Box] Box109  label="Cube097"
  AttacherType = Attacher::AttachEngine3D
  Height = 20
  Length = 26
  Placement = pos=(-13,20,0) rot=(0,0,1;0rad)
  Width = 9
FEATURE [Part::Cut] Cut022020016032007036021
  Base = -> Cut022020016032007036009
  Tool = -> Chamfer027
FEATURE [Part::Cut] Cut022020016032007036022
  Base = -> Cut022020016032007036021
  Tool = -> Box109
FEATURE [Part::Cut] Cut022020016032007036023
  Base = -> Cut022020016032007036022
  Tool = -> Chamfer030006002016005008003006
FEATURE [Part::Fillet] Fillet
  Base = -> Cut022020016032007036023
  Edges = 1 edges r=6.5: [Edge23]
FEATURE [Part::Cut] Cut022020016032007036024
  Base = -> Fillet
  Tool = -> Chamfer028
FEATURE [Part::Cut] Cut022020016032007036025
  Base = -> Cut022020016032007036024
  Tool = -> Box103
FEATURE [Part::Cylinder] Cylinder044  label="idler001"
  Angle = 360
  AttacherType = Attacher::AttachEngine3D
  Height = 10
  Placement = pos=(5,-1.25,10) rot=(0,-1,0;1.5708rad)
  Radius = 2.65
FEATURE [Part::Cut] Cut022020016032007036026  label="idler-template"
  Base = -> Cylinder
  Placement = pos=(0,0,-1) rot=(0,0,1;0rad)
  Tool = -> Cylinder044
FEATURE [Part::Chamfer] Chamfer030006002016005008003009005
  Base = -> Cut022020016032007036025
  Edges = 2 edges r=2: [Edge87,Edge132]
FEATURE [Part::Chamfer] Chamfer030006002016005008003009006
  Base = -> Chamfer030006002016005008003009005
  Edges = 2 edges r=3: [Edge23,Edge135]
FEATURE [Part::Chamfer] Chamfer030006002016005008003009007  label="arm-rev-7"
  Base = -> Chamfer030006002016005008003009006
  Edges = 62 edges r=0.4: [Edge1,Edge2,Edge3,Edge4,Edge5,Edge6,Edge7,Edge8,Edge9,Edge11,Edge12,Edge25,Edge26,Edge28,Edge30,Edge33,Edge35,Edge36,Edge38,Edge39,Edge41,Edge42,Edge43,Edge44,Edge45,Edge46,Edge47,Edge48,Edge50,Edge51,Edge52,Edge55,Edge56,Edge78,Edge82,Edge84,Edge85,Edge86,Edge87,Edge88,Edge89,Edge90,Edge91,Edge92,+18 more]
FEATURE [Part::Cut] Cut022020016032007036027
  Base = -> Fusion010006012010005012005015
  Placement = pos=(0,-4.5,0) rot=(0,0,1;0rad)
  Tool = -> Box107
FEATURE [Part::MultiFuse] Fusion010006012010005012005027012004  label="arm-custom-support"
  Shapes = -> [Cut022020016032007036027,Fusion010006012010005012005017,Fusion010006012010005012005016]
FEATURE [Part::MultiFuse] Fusion010006012010005012005027012006  label="base-rev-7-basic"
  Shapes = -> [Cut022020016006,Cut022020016019,Chamfer030006002016005008003003,Chamfer030006002016005008003004,Cut022020016032007036020]
FEATURE [Part::Feature] Fusion010006012010005012005027012006001  label="base-rev-7-basic001"
  shape: bbox 64 x 40 x 24.4 mm, 132 faces (baked)
FEATURE [Part::Chamfer] Chamfer030006002016005008003009008  label="base-rev-7"
  Base = -> Fusion010006012010005012005027012006001
  Edges = 36 edges r=0.4: [Edge2,Edge4,Edge6,Edge8,Edge9,Edge19,Edge21,Edge22,Edge24,Edge25,Edge28,Edge31,Edge41,Edge43,Edge45,Edge46,Edge67,Edge83,Edge84,Edge86,Edge88,Edge89,Edge91,Edge92,Edge94,Edge125,Edge126,Edge146,Edge147,Edge149,Edge151,Edge163,Edge170,Edge171,Edge172,Edge173]
